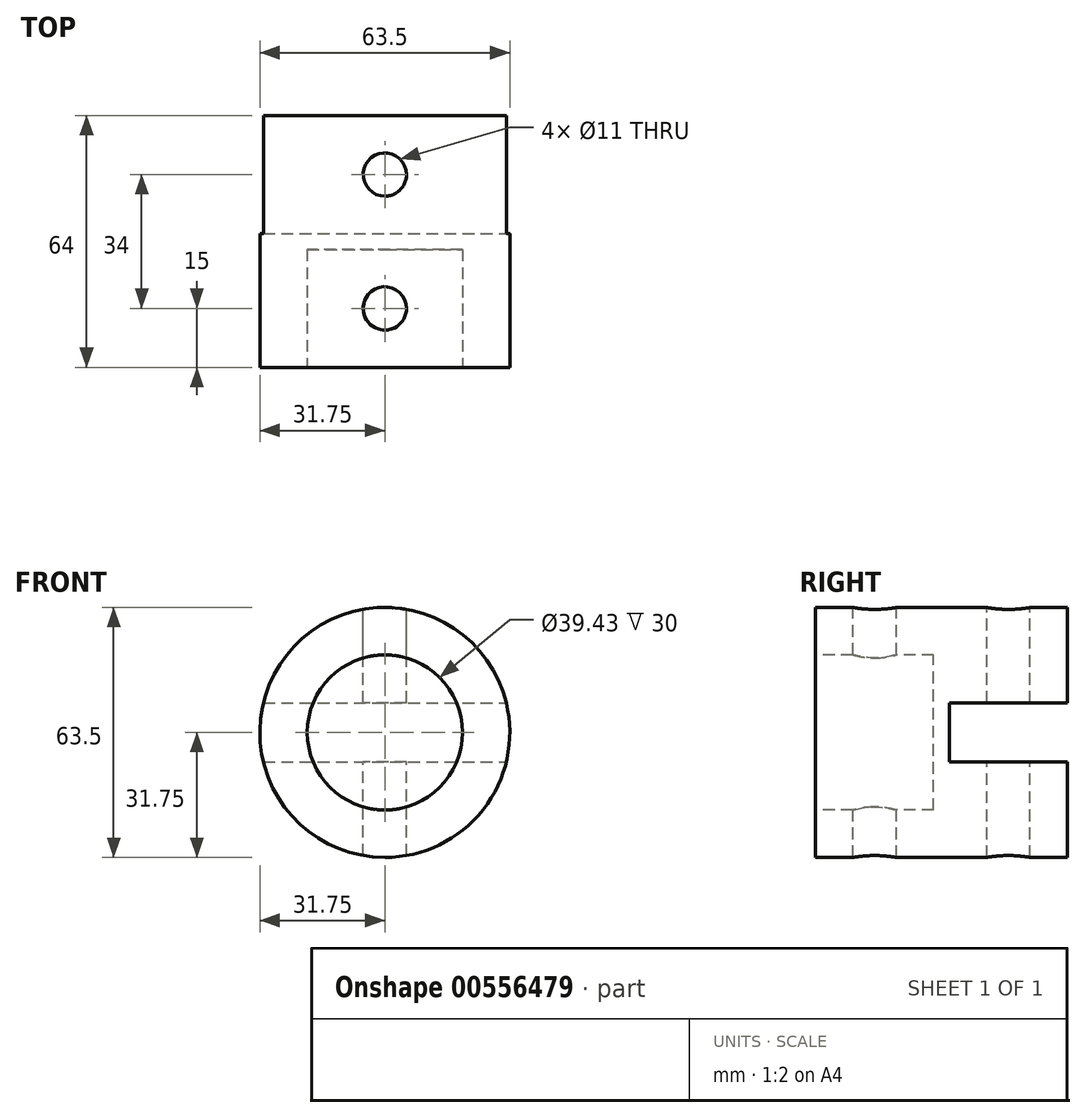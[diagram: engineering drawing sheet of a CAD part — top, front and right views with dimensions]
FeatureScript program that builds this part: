
annotation { "Feature Type Name" : "Feature", "Feature Type Description" : "" }
export const myFeature = defineFeature(function(context is Context, id is Id, definition is map)
    precondition{}
    {
        {
            var Q0;
            Q0=qCreatedBy(makeId("Front.planeOp"),FACE);
            var sketch = newSketch(context, id + "F0", { "sketchPlane" : qUnion([Q0])});
            skCircle(sketch, "E0", {"center": v(0, 0) * mm, "radius": 31.75 * mm});
            skSolve(sketch);
        }
        {
            var Q0;
            Q0=makeQuery(id+"F0.imprint","IMPRINT",FACE,{"disambiguationData":[TD([[makeQuery(id+"F0.imprint","IMPRINT",EDGE,{"derivedFrom":sQuery(id+"F0.wireOp",EDGE,"E0")}),1.0]])]});
            extrude(context, id + "F1", {"entities" : qUnion([Q0]), "depth" : 64 * mm, "offsetDistance" : 25 * mm});
        }
        {
            var Q0;
            Q0=makeQuery(id+"F1.opExtrude","CAP_FACE",FACE,{"disambiguationData":[OSD([sQuery(id+"F0.wireOp",EDGE,"E0")])],"isStart":false});
            var sketch = newSketch(context, id + "F2", { "sketchPlane" : qUnion([Q0])});
            skCircle(sketch, "E1", {"center": v(0, 0) * mm, "radius": 19.71 * mm});
            skSolve(sketch);
        }
        {
            var Q0;
            Q0=makeQuery(id+"F2.imprint","IMPRINT",FACE,{"disambiguationData":[TD([[makeQuery(id+"F2.imprint","IMPRINT",EDGE,{"derivedFrom":sQuery(id+"F2.wireOp",EDGE,"E1")}),1.0]])]});
            extrude(context, id + "F3", {"entities" : qUnion([Q0]), "operationType" : NewBodyOperationType.REMOVE, "oppositeDirection" : true, "depth" : 30 * mm, "offsetDistance" : 25 * mm});
        }
        {
            var Q0;
            Q0=makeQuery(id+"F1.opExtrude","CAP_FACE",FACE,{"disambiguationData":[OSD([sQuery(id+"F0.wireOp",EDGE,"E0")])],"isStart":true});
            var sketch = newSketch(context, id + "F4", { "sketchPlane" : qUnion([Q0])});
            skLineSegment(sketch, "E2.bottom", {"start": v(50, -7.5) * mm, "end": v(-50, -7.5) * mm});
            skLineSegment(sketch, "E2.top", {"start": v(50, 7.5) * mm, "end": v(-50, 7.5) * mm});
            skLineSegment(sketch, "E2.left", {"start": v(50, -7.5) * mm, "end": v(50, 7.5) * mm});
            skLineSegment(sketch, "E2.right", {"start": v(-50, -7.5) * mm, "end": v(-50, 7.5) * mm});
            skPoint(sketch, "E2.middle", {"position": v(0, 0) * mm});
            skSolve(sketch);
        }
        {
            var Q0;
            {var subQ0=sQuery(id+"F4.wireOp",EDGE,"E2.bottom");var subQ1=makeQuery(id+"F1.opExtrude","CAP_EDGE",EDGE,{"disambiguationData":[OSD([sQuery(id+"F0.wireOp",EDGE,"E0")])],"isStart":true});var subQ2=makeQuery(id+"F4.imprint","INTERSECT",VERTEX,{"disambiguationData":[OD(0.0)],"derivedFrom":[subQ1,subQ0]});Q0=makeQuery(id+"F4.imprint","IMPRINT",FACE,{"disambiguationData":[TD([[makeQuery(id+"F4.imprint","IMPRINT",EDGE,{"disambiguationData":[TD([[subQ2,-1.0]])],"derivedFrom":subQ0}),-1.0]])]});}
            extrude(context, id + "F5", {"entities" : qUnion([Q0]), "operationType" : NewBodyOperationType.REMOVE, "oppositeDirection" : true, "depth" : 30 * mm, "offsetDistance" : 25 * mm});
        }
        {
            var Q0;
            Q0=qCreatedBy(makeId("Top.planeOp"),FACE);
            var sketch = newSketch(context, id + "F6", { "sketchPlane" : qUnion([Q0])});
            skCircle(sketch, "E3", {"center": v(0, -49) * mm, "radius": 5.5 * mm});
            skSolve(sketch);
        }
        {
            var Q0;
            Q0=makeQuery(id+"F6.imprint","IMPRINT",FACE,{"disambiguationData":[TD([[makeQuery(id+"F6.imprint","IMPRINT",EDGE,{"derivedFrom":sQuery(id+"F6.wireOp",EDGE,"E3")}),1.0]])]});
            extrude(context, id + "F7", {"entities" : qUnion([Q0]), "operationType" : NewBodyOperationType.REMOVE, "endBound" : BoundingType.SYMMETRIC, "oppositeDirection" : true, "depth" : 70 * mm, "offsetDistance" : 25 * mm});
        }
        {
            var Q0;
            Q0=qCreatedBy(makeId("Top.planeOp"),FACE);
            var sketch = newSketch(context, id + "F8", { "sketchPlane" : qUnion([Q0])});
            skCircle(sketch, "E4", {"center": v(0, -15) * mm, "radius": 5.5 * mm});
            skSolve(sketch);
        }
        {
            var Q0;
            Q0=makeQuery(id+"F8.imprint","IMPRINT",FACE,{"disambiguationData":[TD([[makeQuery(id+"F8.imprint","IMPRINT",EDGE,{"derivedFrom":sQuery(id+"F8.wireOp",EDGE,"E4")}),1.0]])]});
            extrude(context, id + "F9", {"entities" : qUnion([Q0]), "operationType" : NewBodyOperationType.REMOVE, "endBound" : BoundingType.SYMMETRIC, "oppositeDirection" : true, "depth" : 70 * mm, "offsetDistance" : 25 * mm});
        }
        {
            var Q0;
            Q0=sQuery(id+"F0.wireOp",EDGE,"E0");
            extrude(context, id + "F10", {"bodyType" : ToolBodyType.SURFACE, "surfaceEntities" : qUnion([Q0]), "depth" : 25.4 * mm, "offsetDistance" : 25.4 * mm});
        }
    });
